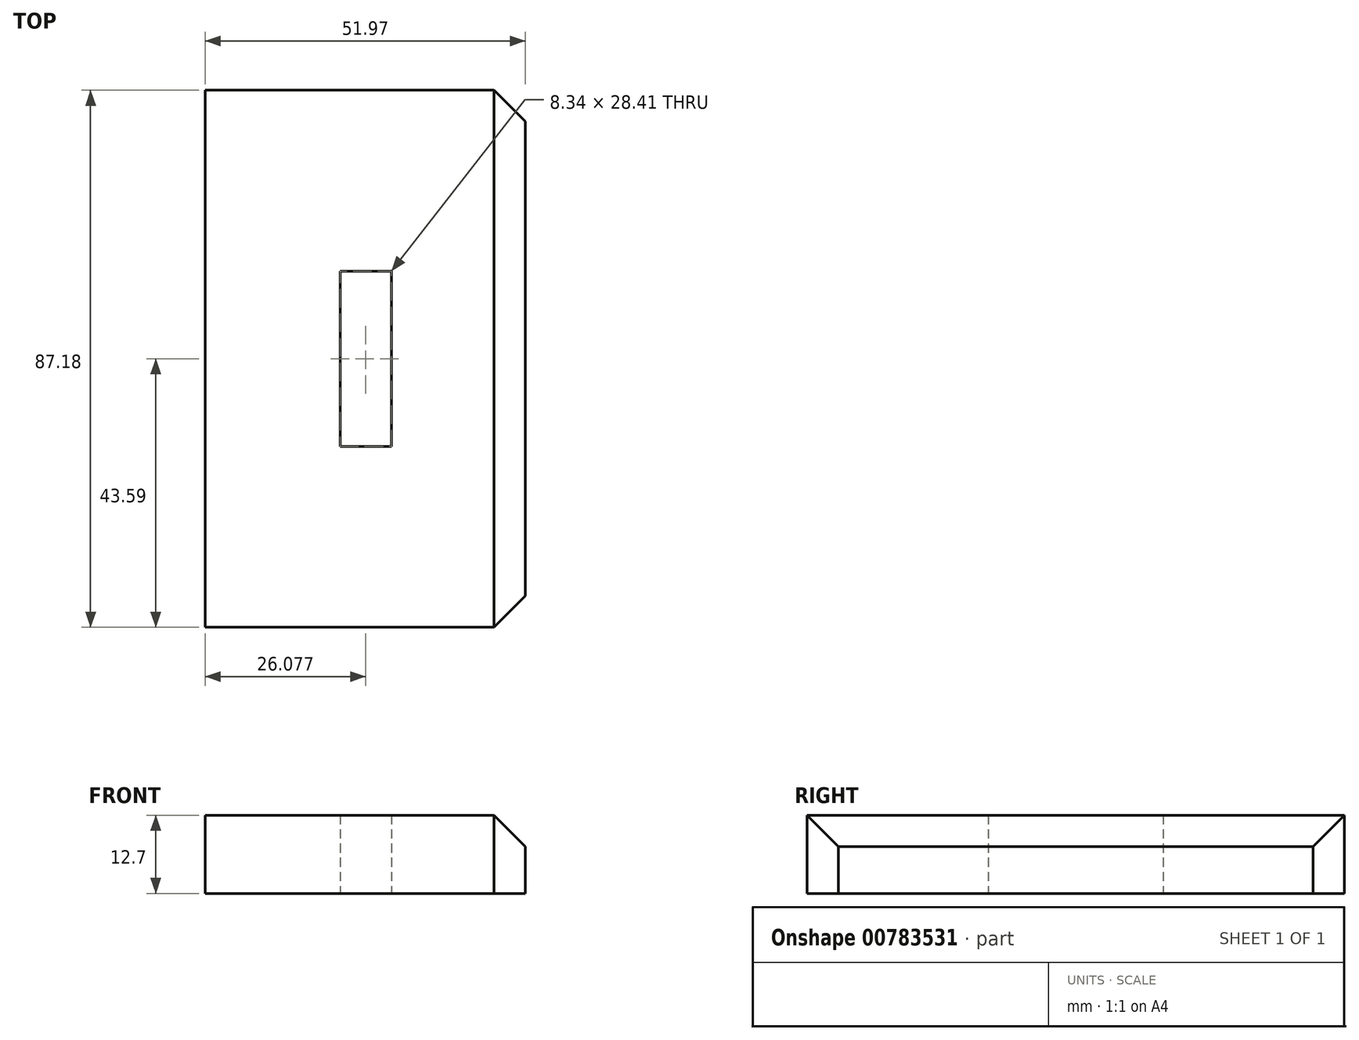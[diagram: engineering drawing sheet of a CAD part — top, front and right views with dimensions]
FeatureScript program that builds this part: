
annotation { "Feature Type Name" : "Feature", "Feature Type Description" : "" }
export const myFeature = defineFeature(function(context is Context, id is Id, definition is map)
    precondition{}
    {
        {
            var Q0;
            Q0=qCreatedBy(makeId("Top.planeOp"),FACE);
            var sketch = newSketch(context, id + "F0", { "sketchPlane" : qUnion([Q0])});
            skLineSegment(sketch, "E0.bottom", {"start": v(11.83, -43.59) * mm, "end": v(-40.14, -43.59) * mm});
            skLineSegment(sketch, "E0.top", {"start": v(11.83, 43.59) * mm, "end": v(-40.14, 43.59) * mm});
            skLineSegment(sketch, "E0.left", {"start": v(11.83, -43.59) * mm, "end": v(11.83, 43.59) * mm});
            skLineSegment(sketch, "E0.right", {"start": v(-40.14, -43.59) * mm, "end": v(-40.14, 43.59) * mm});
            skPoint(sketch, "E0.middle", {"position": v(-14.16, 0) * mm});
            skLineSegment(sketch, "E1.bottom", {"start": v(-9.9, -14.2) * mm, "end": v(-18.23, -14.2) * mm});
            skLineSegment(sketch, "E1.top", {"start": v(-9.9, 14.2) * mm, "end": v(-18.23, 14.2) * mm});
            skLineSegment(sketch, "E1.left", {"start": v(-9.9, -14.2) * mm, "end": v(-9.9, 14.2) * mm});
            skLineSegment(sketch, "E1.right", {"start": v(-18.23, -14.2) * mm, "end": v(-18.23, 14.2) * mm});
            skPoint(sketch, "E1.middle", {"position": v(-14.06, 0) * mm});
            skSolve(sketch);
        }
        {
            var Q0;
            Q0 = qSketchRegion(id + "F0", true);
            extrude(context, id + "F1", {"entities" : qUnion([Q0]), "depth" : 12.7 * mm, "offsetDistance" : 25.4 * mm});
        }
        {
            var Q0;
            Q0=makeQuery(id+"F1.opExtrude","SWEPT_EDGE",EDGE,{"disambiguationData":[OSD([sQuery(id+"F0.wireOp",EDGE,"E0.top"),sQuery(id+"F0.wireOp",EDGE,"E0.left")])]});
            var Q1;
            Q1=makeQuery(id+"F1.opExtrude","CAP_EDGE",EDGE,{"disambiguationData":[OSD([sQuery(id+"F0.wireOp",EDGE,"E0.left")])],"isStart":false});
            var Q2;
            Q2=makeQuery(id+"F1.opExtrude","SWEPT_EDGE",EDGE,{"disambiguationData":[OSD([sQuery(id+"F0.wireOp",EDGE,"E0.bottom"),sQuery(id+"F0.wireOp",EDGE,"E0.left")])]});
            chamfer(context, id + "F2", {"entities" : qUnion([Q0, Q1, Q2]), "width" : 5.08 * mm, "tangentPropagation" : true});
        }
    });
